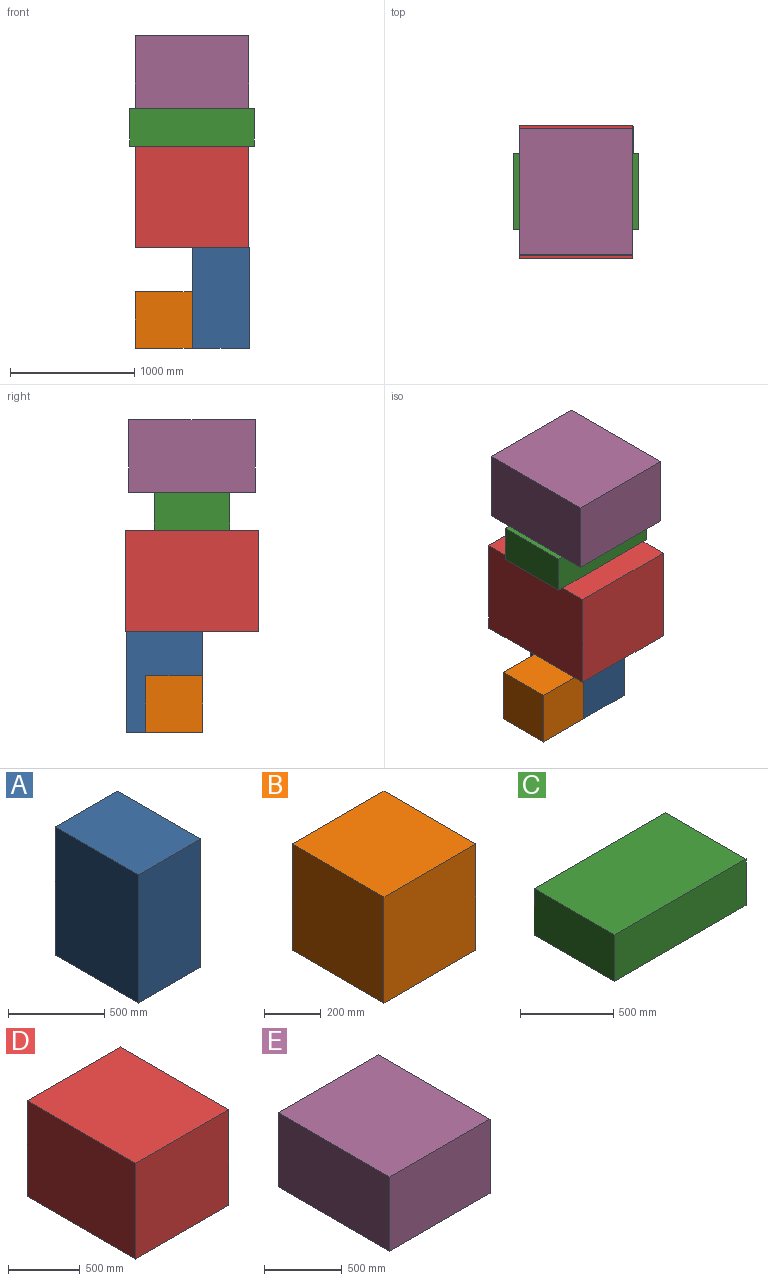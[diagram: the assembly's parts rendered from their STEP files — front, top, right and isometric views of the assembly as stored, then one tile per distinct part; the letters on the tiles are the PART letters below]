
ASSEMBLY  parts=5 mates=5
PART A: 6 faces, bbox 457.2x609.6x812.8 mm
  f0: plane 812.8x457.2mm, normal (0,-1,0), area 371612.2mm2, adj f1,f3,f4,f5
  f1: plane 812.8x609.6mm, normal (1,0,0), area 495482.9mm2, adj f0,f2,f4,f5
  f2: plane 812.8x457.2mm, normal (0,1,0), area 371612.2mm2, adj f1,f3,f4,f5
  f3: plane 812.8x609.6mm, normal (-1,0,0), area 495482.9mm2, adj f0,f2,f4,f5
  f4: plane 609.6x457.2mm, normal (0,0,1), area 278709.1mm2, adj f0,f1,f2,f3
  f5: plane 609.6x457.2mm, normal (0,0,-1), area 278709.1mm2, adj f0,f1,f2,f3
PART B: 6 faces, bbox 457.2x457.2x457.2 mm
  f0: plane 457.2x457.2mm, normal (0,-1,0), area 209031.8mm2, adj f1,f3,f4,f5
  f1: plane 457.2x457.2mm, normal (1,0,0), area 209031.8mm2, adj f0,f2,f4,f5
  f2: plane 457.2x457.2mm, normal (0,1,0), area 209031.8mm2, adj f1,f3,f4,f5
  f3: plane 457.2x457.2mm, normal (-1,0,0), area 209031.8mm2, adj f0,f2,f4,f5
  f4: plane 457.2x457.2mm, normal (0,0,1), area 209031.8mm2, adj f0,f1,f2,f3
  f5: plane 457.2x457.2mm, normal (0,0,-1), area 209031.8mm2, adj f0,f1,f2,f3
PART C: 6 faces, bbox 1000x609.6x304.8 mm
  f0: plane 1000x304.8mm, normal (0,-1,0), area 304800mm2, adj f1,f3,f4,f5
  f1: plane 609.6x304.8mm, normal (1,0,0), area 185806.1mm2, adj f0,f2,f4,f5
  f2: plane 1000x304.8mm, normal (0,1,0), area 304800mm2, adj f1,f3,f4,f5
  f3: plane 609.6x304.8mm, normal (-1,0,0), area 185806.1mm2, adj f0,f2,f4,f5
  f4: plane 1000x609.6mm, normal (0,0,1), area 609600mm2, adj f0,f1,f2,f3
  f5: plane 1000x609.6mm, normal (0,0,-1), area 609600mm2, adj f0,f1,f2,f3
PART D: 6 faces, bbox 914.4x1066.8x812.8 mm
  f0: plane 914.4x812.8mm, normal (0,-1,0), area 743224.3mm2, adj f1,f3,f4,f5
  f1: plane 1066.8x812.8mm, normal (1,0,0), area 867095mm2, adj f0,f2,f4,f5
  f2: plane 914.4x812.8mm, normal (0,1,0), area 743224.3mm2, adj f1,f3,f4,f5
  f3: plane 1066.8x812.8mm, normal (-1,0,0), area 867095mm2, adj f0,f2,f4,f5
  f4: plane 1066.8x914.4mm, normal (0,0,1), area 975481.9mm2, adj f0,f1,f2,f3
  f5: plane 1066.8x914.4mm, normal (0,0,-1), area 975481.9mm2, adj f0,f1,f2,f3
PART E: 6 faces, bbox 914.4x1016x584.2 mm
  f0: plane 914.4x584.2mm, normal (0,-1,0), area 534192.5mm2, adj f1,f3,f4,f5
  f1: plane 1016x584.2mm, normal (1,0,0), area 593547.2mm2, adj f0,f2,f4,f5
  f2: plane 914.4x584.2mm, normal (0,1,0), area 534192.5mm2, adj f1,f3,f4,f5
  f3: plane 1016x584.2mm, normal (-1,0,0), area 593547.2mm2, adj f0,f2,f4,f5
  f4: plane 1016x914.4mm, normal (0,0,1), area 929030.4mm2, adj f0,f1,f2,f3
  f5: plane 1016x914.4mm, normal (0,0,-1), area 929030.4mm2, adj f0,f1,f2,f3
PLACE A t=(-506.46,-809.67,-634.38)mm
PLACE B t=(-967.11,-885.87,-634.38)mm
PLACE C t=(-739.63,-1029.81,991.22)mm
PLACE D t=(-739.63,-1029.81,178.42)mm
PLACE E t=(-739.63,-1029.81,1296.02)mm
MATE planar E.f5 <-> C.f4  axis (0,0,-1) through (-739.63,-1029.81,1296.02)mm
MATE planar A.f0 <-> B.f0  axis (0,-1,0) through (-506.46,-1114.47,-227.98)mm
MATE planar B.f5 <-> A.f5  axis (0,0,-1) through (-967.11,-885.87,-634.38)mm
MATE planar A.f4 <-> D.f5  axis (0,0,1) through (-506.46,-809.67,178.42)mm
MATE planar C.f5 <-> D.f4  axis (0,0,-1) through (-739.63,-1029.81,991.22)mm
